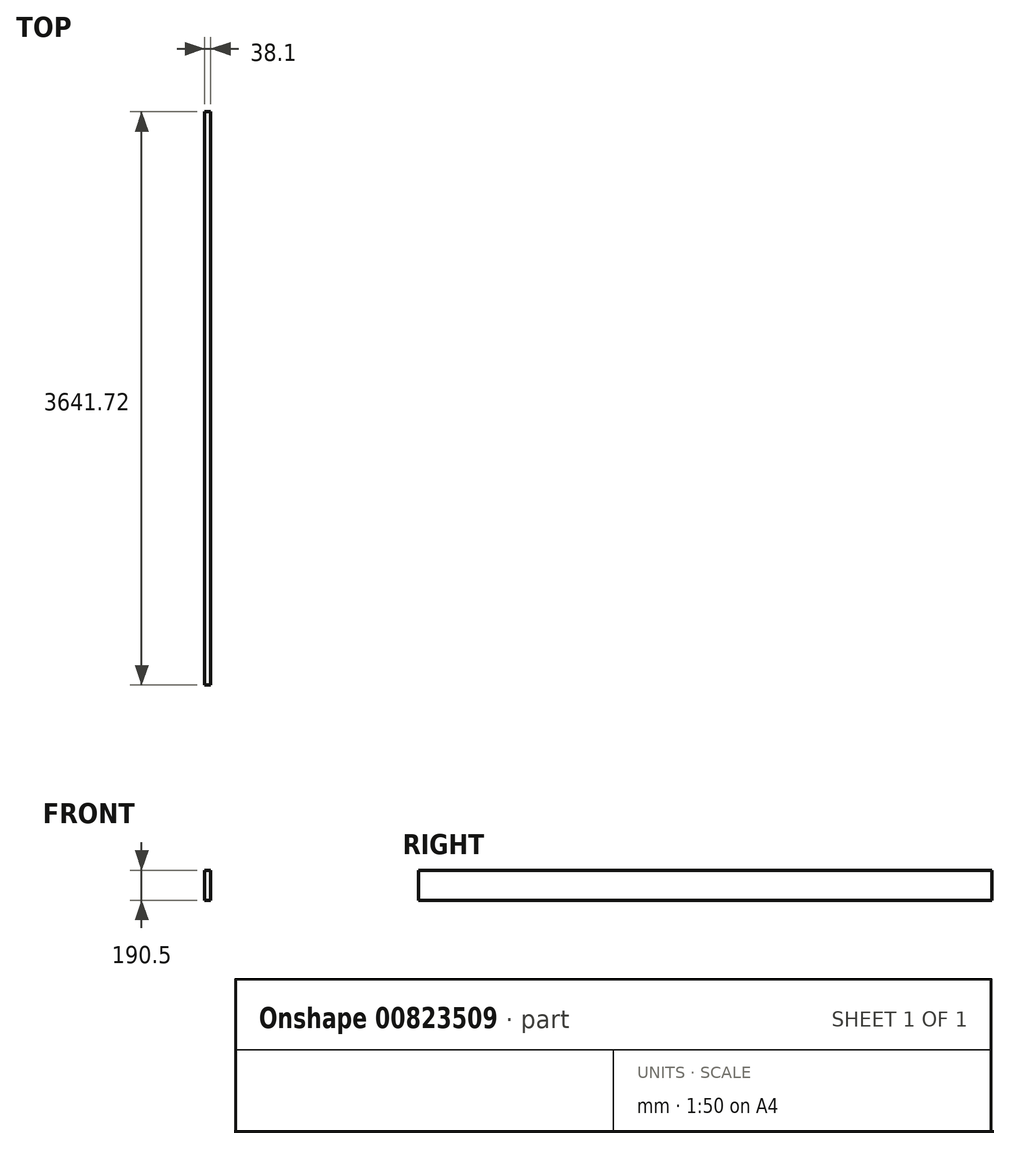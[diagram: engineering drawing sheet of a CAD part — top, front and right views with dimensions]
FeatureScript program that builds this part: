
annotation { "Feature Type Name" : "Feature", "Feature Type Description" : "" }
export const myFeature = defineFeature(function(context is Context, id is Id, definition is map)
    precondition{}
    {
        {
            var Q0;
            Q0=qCreatedBy(makeId("Front.planeOp"),FACE);
            var sketch = newSketch(context, id + "F0", { "sketchPlane" : qUnion([Q0])});
            skLineSegment(sketch, "E0.bottom", {"start": v(0, 0) * mm, "end": v(38.1, 0) * mm});
            skLineSegment(sketch, "E0.top", {"start": v(0, 190.5) * mm, "end": v(38.1, 190.5) * mm});
            skLineSegment(sketch, "E0.left", {"start": v(0, 0) * mm, "end": v(0, 190.5) * mm});
            skLineSegment(sketch, "E0.right", {"start": v(38.1, 0) * mm, "end": v(38.1, 190.5) * mm});
            skSolve(sketch);
        }
        {
            var Q0;
            Q0=qSketchRegion(id+"F0",true);
            extrude(context, id + "F1", {"entities" : qUnion([Q0]), "depth" : 3641.72 * mm, "offsetDistance" : 25.4 * mm});
        }
    });
